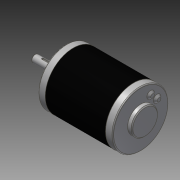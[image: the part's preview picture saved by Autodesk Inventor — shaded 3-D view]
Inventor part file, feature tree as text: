
AUTODESK INVENTOR PART (.ipt)
format: ipt  version: 2014 SP1 (Build 180222100, 222)  size: 165,888 bytes
history: native  units: in
note: dims shown in document units (in); Inventor stores cm internally (conversion verified against a paired STEP export)
features: chamfer x1, other x1, imported_body x1
ambient origin geometry x8: Origin, YZ Plane, XZ Plane, XY Plane, X Axis, Y Axis, Z Axis, Center Point
bodies: Body1 (feature_tree)
feature tree (3):
  chamfer  "Chamfer3"  [1 undecoded]
  other  "217-3371-STEP1"
  imported_body  "Base1"
note: 1 required parameter value undecoded (feature->parameter linkage not recoverable at this tier; creation-order binding heuristic only, values carry confidence <= 0.55)
